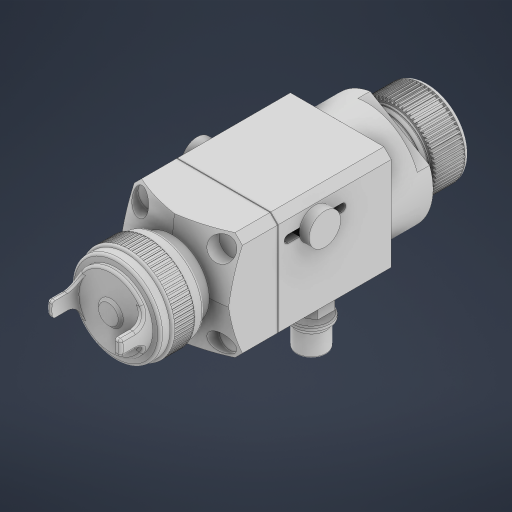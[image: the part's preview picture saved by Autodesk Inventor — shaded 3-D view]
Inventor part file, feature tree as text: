
AUTODESK INVENTOR PART (.ipt)
format: ipt  version: 2024 (Build 280153000, 153)  size: 1,246,720 bytes
history: native  units: in
note: dims shown in document units (in); Inventor stores cm internally (conversion verified against a paired STEP export)
features: other x2, extrude x2, sketch x2
ambient origin geometry x8: Origin, YZ Plane, XZ Plane, XY Plane, X Axis, Y Axis, Z Axis, Center Point
bodies: Body1 (feature_tree)
feature tree (6):
  other  "Sólido1"
  extrude  "Extrusión1"  Depth=0.1575in TaperAngle=0.0deg
  extrude  "Extrusión2"  [1 undecoded]
  sketch  "Boceto2"  dims[d0=0.1575in d1=0.0in d2=0.1575in d3=0.0in]
  sketch  "Boceto3"
  other  "Kes-Ekstrüzyon19"
note: 1 required parameter value undecoded (feature->parameter linkage not recoverable at this tier; creation-order binding heuristic only, values carry confidence <= 0.55)
